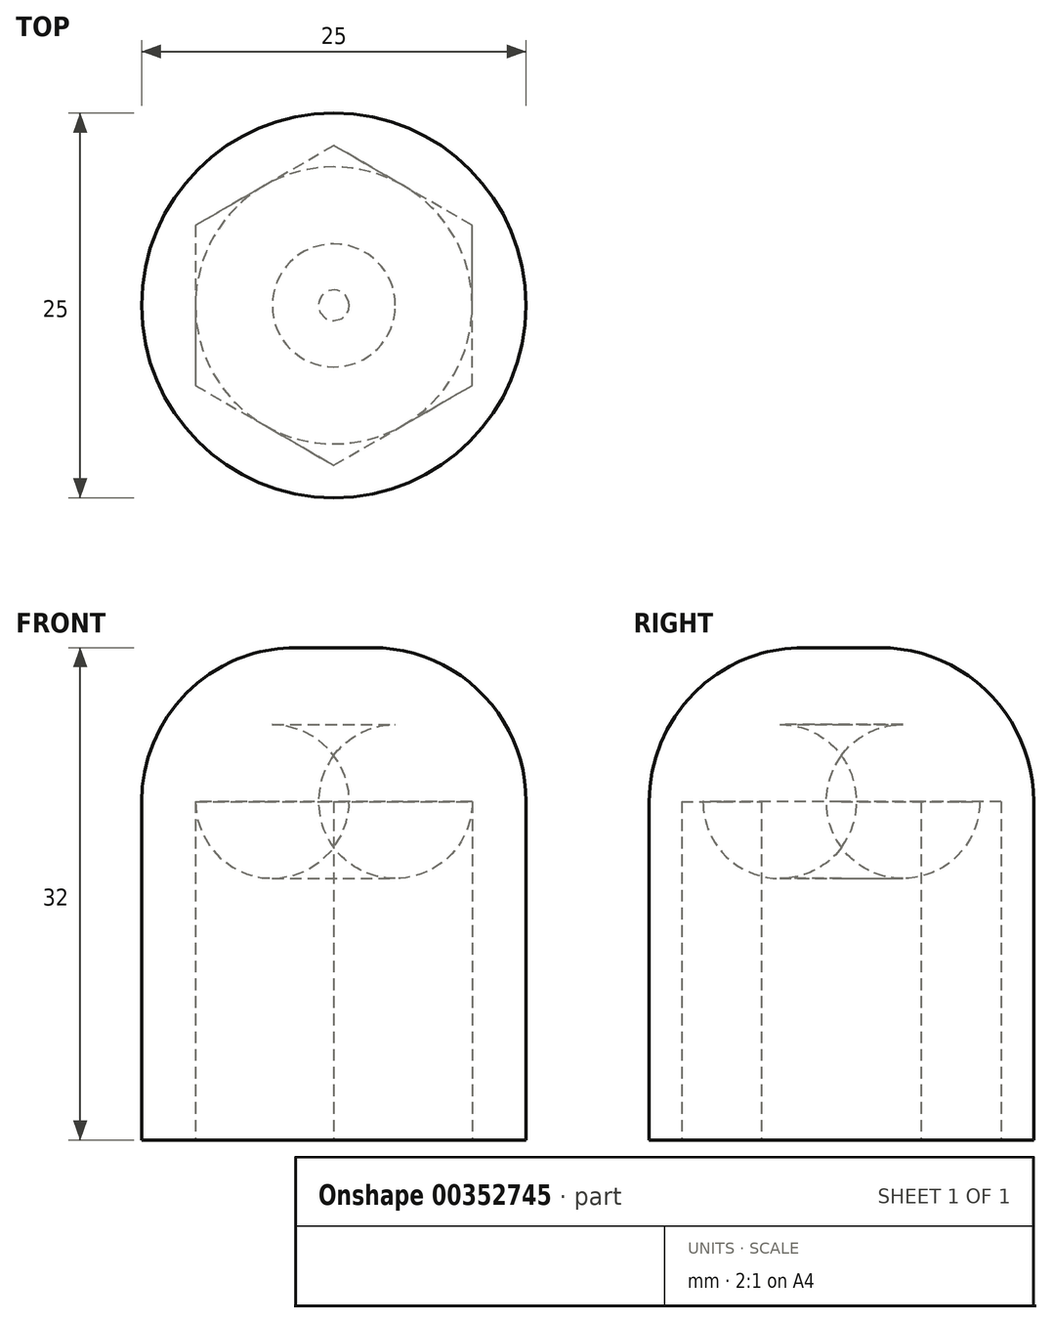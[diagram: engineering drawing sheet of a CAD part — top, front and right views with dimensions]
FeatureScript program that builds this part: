
annotation { "Feature Type Name" : "Feature", "Feature Type Description" : "" }
export const myFeature = defineFeature(function(context is Context, id is Id, definition is map)
    precondition{}
    {
        {
            var Q0;
            Q0=qCreatedBy(makeId("Top.planeOp"),FACE);
            var sketch = newSketch(context, id + "F0", { "sketchPlane" : qUnion([Q0])});
            skCircle(sketch, "E0", {"center": v(0, 0) * mm, "radius": 12.5 * mm});
            skSolve(sketch);
        }
        {
            var Q0;
            Q0=makeQuery(id+"F0.imprint","IMPRINT",FACE,{"disambiguationData":[TD([[makeQuery(id+"F0.imprint","IMPRINT",EDGE,{"derivedFrom":sQuery(id+"F0.wireOp",EDGE,"E0")}),1.0]])]});
            extrude(context, id + "F1", {"entities" : qUnion([Q0]), "depth" : 22 * mm});
        }
        {
            var Q0;
            Q0=makeQuery(id+"F1.opExtrude","CAP_FACE",FACE,{"disambiguationData":[OSD([sQuery(id+"F0.wireOp",EDGE,"E0")])],"isStart":true});
            var sketch = newSketch(context, id + "F2", { "sketchPlane" : qUnion([Q0])});
            skCircle(sketch, "E1.cCircle", {"center": v(0, 0) * mm, "radius": 9 * mm, "construction": true});
            skLineSegment(sketch, "E1.0", {"start": v(9, 5.2) * mm, "end": v(9, -5.2) * mm});
            skLineSegment(sketch, "E1.1", {"start": v(9, -5.2) * mm, "end": v(0, -10.4) * mm});
            skLineSegment(sketch, "E1.2", {"start": v(0, -10.4) * mm, "end": v(-9, -5.2) * mm});
            skLineSegment(sketch, "E1.3", {"start": v(-9, -5.2) * mm, "end": v(-9, 5.2) * mm});
            skLineSegment(sketch, "E1.4", {"start": v(-9, 5.2) * mm, "end": v(0, 10.4) * mm});
            skLineSegment(sketch, "E1.5", {"start": v(0, 10.4) * mm, "end": v(9, 5.2) * mm});
            skPoint(sketch, "E1.0.midPoint", {"position": v(9, 0) * mm});
            skSolve(sketch);
        }
        {
            var Q0;
            Q0=makeQuery(id+"F2.imprint","IMPRINT",FACE,{"disambiguationData":[TD([[makeQuery(id+"F2.imprint","IMPRINT",EDGE,{"derivedFrom":sQuery(id+"F2.wireOp",EDGE,"E1.0")}),-1.0]])]});
            extrude(context, id + "F3", {"entities" : qUnion([Q0]), "operationType" : NewBodyOperationType.REMOVE, "endBound" : BoundingType.UP_TO_NEXT, "oppositeDirection" : true, "depth" : 25 * mm});
        }
        {
            var Q0;
            Q0=makeQuery(id+"F1.opExtrude","CAP_FACE",FACE,{"disambiguationData":[OSD([sQuery(id+"F0.wireOp",EDGE,"E0")])],"isStart":false});
            var sketch = newSketch(context, id + "F4", { "sketchPlane" : qUnion([Q0])});
            skCircle(sketch, "E2", {"center": v(0, 0) * mm, "radius": 12.5 * mm});
            skSolve(sketch);
        }
        {
            var Q0;
            Q0 = qSketchRegion(id + "F4", true);
            extrude(context, id + "F5", {"entities" : qUnion([Q0]), "operationType" : NewBodyOperationType.ADD, "depth" : 10 * mm});
        }
        {
            var Q0;
            Q0=makeQuery(id+"F5.opExtrude","CAP_EDGE",EDGE,{"disambiguationData":[OSD([sQuery(id+"F4.wireOp",EDGE,"E2")])],"isStart":false});
            fillet(context, id + "F6", {"entities" : qUnion([Q0]), "radius" : 10 * mm, "tangentPropagation" : true, "allowEdgeOverflow" : false});
        }
        {
            var Q0;
            Q0=makeQuery(id+"F5.opExtrude","CAP_FACE",FACE,{"disambiguationData":[OSD([sQuery(id+"F4.wireOp",EDGE,"E2")])],"isStart":true});
            var sketch = newSketch(context, id + "F7", { "sketchPlane" : qUnion([Q0])});
            skCircle(sketch, "E3", {"center": v(0, 0) * mm, "radius": 9 * mm});
            skSolve(sketch);
        }
        {
            var Q0;
            {var subQ0=sQuery(id+"F7.wireOp",EDGE,"E3");var subQ1=makeQuery(id+"F1.opExtrude","CAP_FACE",FACE,{"disambiguationData":[OSD([sQuery(id+"F0.wireOp",EDGE,"E0")])],"isStart":false});var subQ5=makeQuery(id+"F7.imprint","INTERSECT",VERTEX,{"derivedFrom":[makeQuery(id+"F3.boolean.opBoolean","COPY",EDGE,{"derivedFrom":makeQuery(id+"F3.opExtrude","TWEAK_EDGE",EDGE,{"derivedFrom":[subQ1,makeQuery(id+"F2.imprint","IMPRINT",EDGE,{"derivedFrom":sQuery(id+"F2.wireOp",EDGE,"E1.5")})]})}),subQ0]});Q0=makeQuery(id+"F7.imprint","IMPRINT",FACE,{"disambiguationData":[TD([[makeQuery(id+"F7.imprint","IMPRINT",EDGE,{"disambiguationData":[TD([[subQ5,1.0]])],"derivedFrom":subQ0}),1.0]])]});}
            extrude(context, id + "F8", {"entities" : qUnion([Q0]), "operationType" : NewBodyOperationType.REMOVE, "oppositeDirection" : true, "depth" : 5 * mm});
        }
        {
            var Q0;
            Q0=makeQuery(id+"F8.boolean.opBoolean","COPY",EDGE,{"derivedFrom":makeQuery(id+"F8.opExtrude","CAP_EDGE",EDGE,{"disambiguationData":[OSD([sQuery(id+"F7.wireOp",EDGE,"E3")])],"isStart":false})});
            fillet(context, id + "F9", {"entities" : qUnion([Q0]), "radius" : 5 * mm, "tangentPropagation" : true, "allowEdgeOverflow" : false});
        }
    });
